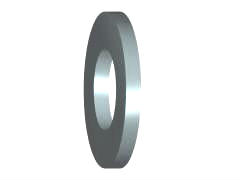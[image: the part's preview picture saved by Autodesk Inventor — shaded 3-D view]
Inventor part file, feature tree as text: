
AUTODESK INVENTOR PART (.ipt)
format: ipt  version: unknown  size: 217,088 bytes
history: native  units: mm (DEFAULTED — no unit token found)
features: extrude x1, other x1, plane x1
ambient origin geometry x7: Origin, YZ Plane, XY Plane, X Axis, Y Axis, Z Axis, Center Point
feature tree (3):
  extrude  "Körper"  Depth=3.0mm
  other  "Work Axis1"
  plane  "Work Plane1"
